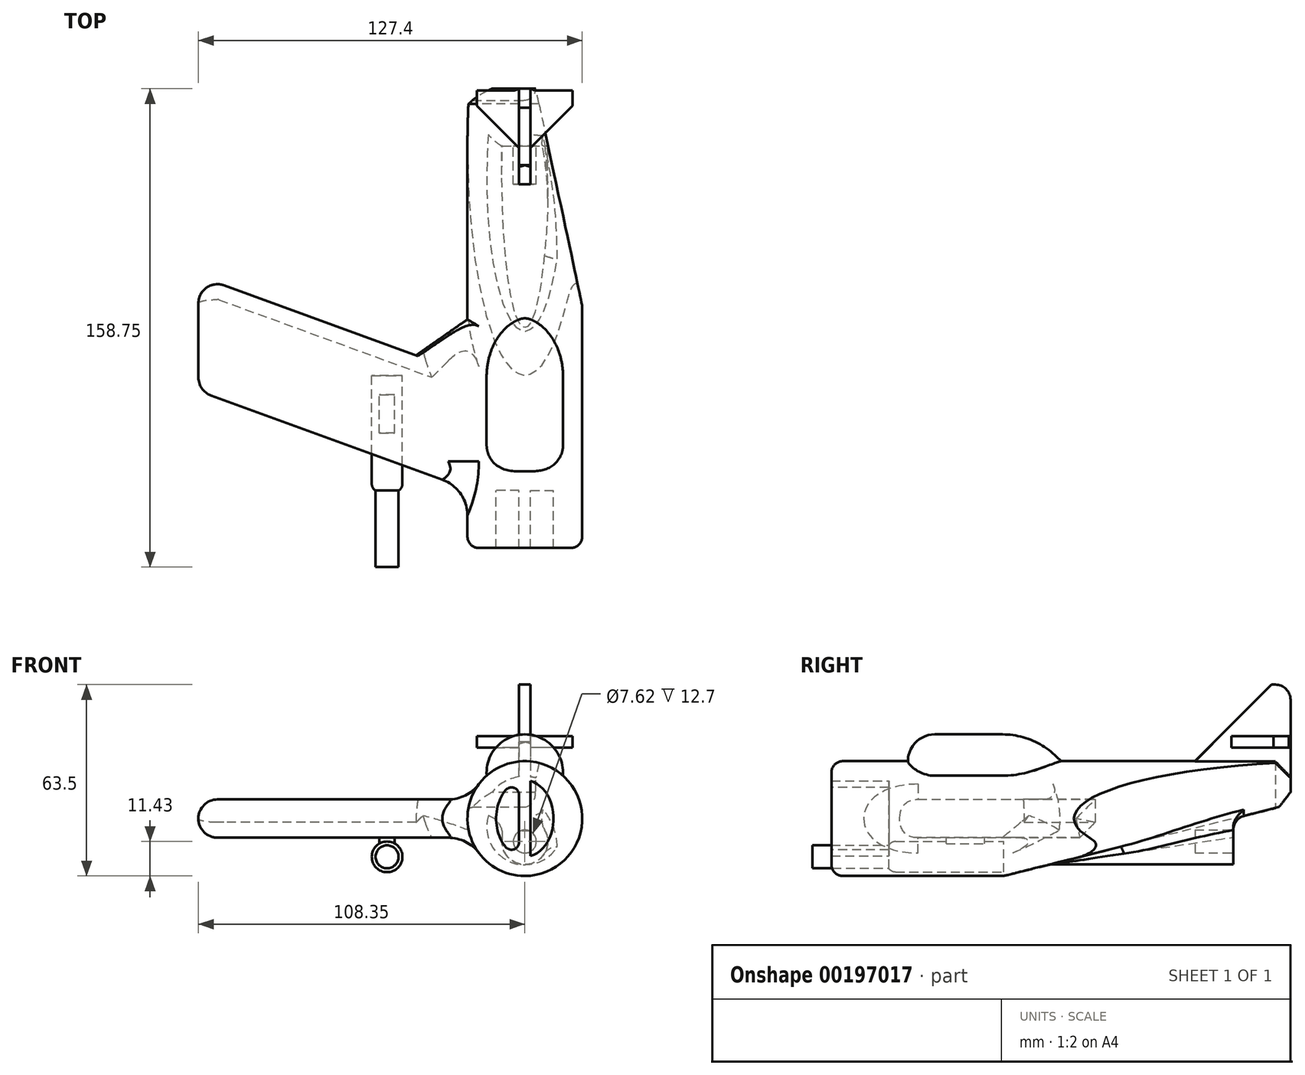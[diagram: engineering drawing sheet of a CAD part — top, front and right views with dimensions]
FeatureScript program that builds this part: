
annotation { "Feature Type Name" : "Feature", "Feature Type Description" : "" }
export const myFeature = defineFeature(function(context is Context, id is Id, definition is map)
    precondition{}
    {
        {
            var Q0;
            Q0=qCreatedBy(makeId("Front.planeOp"),FACE);
            var sketch = newSketch(context, id + "F0", { "sketchPlane" : qUnion([Q0])});
            skCircle(sketch, "E0", {"center": v(0, 0) * mm, "radius": 19.05 * mm});
            skSolve(sketch);
        }
        {
            var Q0;
            Q0=makeQuery(id+"F0.imprint","IMPRINT",FACE,{"disambiguationData":[TD([[makeQuery(id+"F0.imprint","IMPRINT",EDGE,{"derivedFrom":sQuery(id+"F0.wireOp",EDGE,"E0")}),1.0]])]});
            extrude(context, id + "F1", {"entities" : qUnion([Q0]), "endBound" : BoundingType.SYMMETRIC, "depth" : 152.4 * mm});
        }
        {
            var Q0;
            Q0=qCreatedBy(makeId("Top.planeOp"),FACE);
            var sketch = newSketch(context, id + "F2", { "sketchPlane" : qUnion([Q0])});
            skLineSegment(sketch, "E1", {"start": v(0, -25.4) * mm, "end": v(0, -63.5) * mm});
            skLineSegment(sketch, "E2", {"start": v(0, -63.5) * mm, "end": v(-108.35, -24.06) * mm});
            skLineSegment(sketch, "E3", {"start": v(-108.35, -24.06) * mm, "end": v(-108.35, 14.04) * mm});
            skLineSegment(sketch, "E4", {"start": v(-108.35, 14.04) * mm, "end": v(0, -25.4) * mm});
            skSolve(sketch);
        }
        {
            var Q0;
            Q0 = qSketchRegion(id + "F2", true);
            extrude(context, id + "F3", {"entities" : qUnion([Q0]), "operationType" : NewBodyOperationType.ADD, "endBound" : BoundingType.SYMMETRIC, "depth" : 12.7 * mm});
        }
        {
            var Q0;
            Q0=makeQuery(id+"F3.opExtrude","CAP_EDGE",EDGE,{"disambiguationData":[OSD([sQuery(id+"F2.wireOp",EDGE,"E2")])],"isStart":false});
            var Q1;
            Q1=makeQuery(id+"F3.opExtrude","CAP_EDGE",EDGE,{"disambiguationData":[OSD([sQuery(id+"F2.wireOp",EDGE,"E2")])],"isStart":true});
            var Q2;
            Q2=makeQuery(id+"F3.opExtrude","SWEPT_FACE",FACE,{"disambiguationData":[OSD([sQuery(id+"F2.wireOp",EDGE,"E3")])]});
            fillet(context, id + "F4", {"entities" : qUnion([Q0, Q1, Q2]), "radius" : 6.35 * mm, "tangentPropagation" : true, "allowEdgeOverflow" : false});
        }
        {
            var Q0;
            Q0=makeQuery(id+"F3.opExtrude","CAP_EDGE",EDGE,{"disambiguationData":[OSD([sQuery(id+"F2.wireOp",EDGE,"E4")])],"isStart":true});
            chamfer(context, id + "F5", {"entities" : qUnion([Q0]), "width" : 5.08 * mm, "tangentPropagation" : true});
        }
        {
            var Q0;
            Q0=qCreatedBy(makeId("Right.planeOp"),FACE);
            var sketch = newSketch(context, id + "F6", { "sketchPlane" : qUnion([Q0])});
            skLineSegment(sketch, "E5", {"start": v(82.55, 6.35) * mm, "end": v(82.55, -25.4) * mm});
            skLineSegment(sketch, "E6", {"start": v(82.55, -25.4) * mm, "end": v(-44.45, -25.4) * mm});
            skLineSegment(sketch, "E7", {"start": v(-44.45, -25.4) * mm, "end": v(82.55, 6.35) * mm});
            skSolve(sketch);
        }
        {
            var Q0;
            Q0 = qSketchRegion(id + "F6", true);
            extrude(context, id + "F7", {"entities" : qUnion([Q0]), "operationType" : NewBodyOperationType.REMOVE, "endBound" : BoundingType.SYMMETRIC, "depth" : 76.2 * mm});
        }
        {
            var Q0;
            Q0=qCreatedBy(makeId("Front.planeOp"),FACE);
            var sketch = newSketch(context, id + "F8", { "sketchPlane" : qUnion([Q0])});
            skCircle(sketch, "E8", {"center": v(0, 15.24) * mm, "radius": 12.7 * mm});
            skSolve(sketch);
        }
        {
            var Q0;
            Q0=makeQuery(id+"F8.imprint","IMPRINT",FACE,{"disambiguationData":[TD([[makeQuery(id+"F8.imprint","IMPRINT",EDGE,{"derivedFrom":sQuery(id+"F8.wireOp",EDGE,"E8")}),1.0]])]});
            extrude(context, id + "F9", {"entities" : qUnion([Q0]), "operationType" : NewBodyOperationType.ADD, "depth" : 50.8 * mm});
        }
        {
            var Q0;
            Q0=makeQuery(id+"F9.opExtrude","CAP_EDGE",EDGE,{"disambiguationData":[OSD([sQuery(id+"F8.wireOp",EDGE,"E8")])],"isStart":true});
            chamfer(context, id + "F10", {"entities" : qUnion([Q0]), "width" : 8.9 * mm, "tangentPropagation" : true});
        }
        {
            var Q0;
            Q0=makeQuery(id+"F9.opExtrude","CAP_EDGE",EDGE,{"disambiguationData":[OSD([sQuery(id+"F8.wireOp",EDGE,"E8")])],"isStart":false});
            fillet(context, id + "F11", {"entities" : qUnion([Q0]), "radius" : 8.9 * mm, "tangentPropagation" : true, "allowEdgeOverflow" : false});
        }
        {
            var Q0;
            {var subQ0=sQuery(id+"F8.wireOp",EDGE,"E8");Q0=makeQuery(id+"F10.opChamfer","BLEND_EDGE",EDGE,{"blendedFrom":[makeQuery(id+"F9.opExtrude","CAP_EDGE",EDGE,{"disambiguationData":[OSD([subQ0])],"isStart":true}),makeQuery(id+"F9.opExtrude","SWEPT_FACE",FACE,{"disambiguationData":[OSD([subQ0])]})],"blendedInto":[makeQuery(id+"F9.opExtrude","SWEPT_FACE",FACE,{"disambiguationData":[OSD([subQ0])]})]});}
            fillet(context, id + "F12", {"entities" : qUnion([Q0]), "radius" : 25.4 * mm, "tangentPropagation" : true, "allowEdgeOverflow" : false});
        }
        {
            var Q0;
            Q0=makeQuery(id+"F1.opExtrude","CAP_FACE",FACE,{"disambiguationData":[OSD([sQuery(id+"F0.wireOp",EDGE,"E0")])],"isStart":true});
            var sketch = newSketch(context, id + "F13", { "sketchPlane" : qUnion([Q0])});
            skLineSegment(sketch, "E9.bottom", {"start": v(-1.9, 44.45) * mm, "end": v(1.9, 44.45) * mm});
            skLineSegment(sketch, "E9.top", {"start": v(-1.9, 6.35) * mm, "end": v(1.9, 6.35) * mm});
            skLineSegment(sketch, "E9.left", {"start": v(-1.9, 44.45) * mm, "end": v(-1.9, 6.35) * mm});
            skLineSegment(sketch, "E9.right", {"start": v(1.9, 44.45) * mm, "end": v(1.9, 6.35) * mm});
            skPoint(sketch, "E9.middle", {"position": v(0, 25.4) * mm});
            skSolve(sketch);
        }
        {
            var Q0;
            Q0 = qSketchRegion(id + "F13", true);
            extrude(context, id + "F14", {"entities" : qUnion([Q0]), "operationType" : NewBodyOperationType.ADD, "oppositeDirection" : true, "depth" : 25.4 * mm});
        }
        {
            var Q0;
            Q0=makeQuery(id+"F14.opExtrude","CAP_EDGE",EDGE,{"disambiguationData":[OSD([sQuery(id+"F13.wireOp",EDGE,"E9.bottom")])],"isStart":false});
            chamfer(context, id + "F15", {"entities" : qUnion([Q0]), "width" : 19.05 * mm, "tangentPropagation" : true});
        }
        {
            var Q0;
            Q0=makeQuery(id+"F14.opExtrude","CAP_EDGE",EDGE,{"disambiguationData":[OSD([sQuery(id+"F13.wireOp",EDGE,"E9.bottom")])],"isStart":true});
            fillet(context, id + "F16", {"entities" : qUnion([Q0]), "radius" : 5.08 * mm, "tangentPropagation" : true, "allowEdgeOverflow" : false});
        }
        {
            var Q0;
            Q0=qCreatedBy(makeId("Right.planeOp"),FACE);
            var sketch = newSketch(context, id + "F17", { "sketchPlane" : qUnion([Q0])});
            skLineSegment(sketch, "E10.bottom", {"start": v(75.56, 27.3) * mm, "end": v(56.52, 27.3) * mm});
            skLineSegment(sketch, "E10.top", {"start": v(75.57, 23.5) * mm, "end": v(56.52, 23.5) * mm});
            skLineSegment(sketch, "E10.left", {"start": v(75.57, 27.3) * mm, "end": v(75.57, 23.5) * mm});
            skLineSegment(sketch, "E10.right", {"start": v(56.52, 27.3) * mm, "end": v(56.52, 23.5) * mm});
            skPoint(sketch, "E10.middle", {"position": v(66.04, 25.4) * mm});
            skSolve(sketch);
        }
        {
            var Q0;
            Q0 = qSketchRegion(id + "F17", true);
            extrude(context, id + "F18", {"entities" : qUnion([Q0]), "operationType" : NewBodyOperationType.ADD, "endBound" : BoundingType.SYMMETRIC, "depth" : 31.75 * mm});
        }
        {
            var Q0;
            Q0=makeQuery(id+"F18.opExtrude","CAP_EDGE",EDGE,{"disambiguationData":[OSD([sQuery(id+"F17.wireOp",EDGE,"E10.right")])],"isStart":true});
            var Q1;
            Q1=makeQuery(id+"F18.opExtrude","CAP_EDGE",EDGE,{"disambiguationData":[OSD([sQuery(id+"F17.wireOp",EDGE,"E10.right")])],"isStart":false});
            chamfer(context, id + "F19", {"entities" : qUnion([Q0, Q1]), "width" : 13.97 * mm, "tangentPropagation" : true});
        }
        {
            var Q0;
            Q0=makeQuery(id+"F1.opExtrude","CAP_FACE",FACE,{"disambiguationData":[OSD([sQuery(id+"F0.wireOp",EDGE,"E0")])],"isStart":false});
            var sketch = newSketch(context, id + "F20", { "sketchPlane" : qUnion([Q0])});
            skEllipse(sketch, "E11", {"center": v(0, 0) * mm, "majorRadius": 12.7 * mm, "minorRadius": 9.53 * mm, "majorAxis": v(0, 1)});
            skSolve(sketch);
        }
        {
            var Q0;
            Q0=makeQuery(id+"F20.imprint","IMPRINT",FACE,{"disambiguationData":[TD([[makeQuery(id+"F20.imprint","IMPRINT",EDGE,{"derivedFrom":sQuery(id+"F20.wireOp",EDGE,"E11")}),1.0]])]});
            extrude(context, id + "F21", {"entities" : qUnion([Q0]), "operationType" : NewBodyOperationType.REMOVE, "oppositeDirection" : true, "depth" : 25.4 * mm});
        }
        {
            var Q0;
            Q0=makeQuery(id+"F1.opExtrude","CAP_EDGE",EDGE,{"disambiguationData":[OSD([sQuery(id+"F0.wireOp",EDGE,"E0")])],"isStart":false});
            fillet(context, id + "F22", {"entities" : qUnion([Q0]), "radius" : 3.8 * mm, "tangentPropagation" : true, "allowEdgeOverflow" : false});
        }
        {
            var Q0;
            Q0=makeQuery(id+"F21.boolean.opBoolean","COPY",FACE,{"derivedFrom":makeQuery(id+"F21.opExtrude","CAP_FACE",FACE,{"disambiguationData":[OSD([sQuery(id+"F20.wireOp",EDGE,"E11")])],"isStart":false})});
            var sketch = newSketch(context, id + "F23", { "sketchPlane" : qUnion([Q0])});
            skLineSegment(sketch, "E12.bottom", {"start": v(1.9, 15.24) * mm, "end": v(-1.9, 15.24) * mm});
            skLineSegment(sketch, "E12.top", {"start": v(1.9, -15.24) * mm, "end": v(-1.9, -15.24) * mm});
            skLineSegment(sketch, "E12.left", {"start": v(1.9, 15.24) * mm, "end": v(1.9, -15.24) * mm});
            skLineSegment(sketch, "E12.right", {"start": v(-1.9, 15.24) * mm, "end": v(-1.9, -15.24) * mm});
            skPoint(sketch, "E12.middle", {"position": v(0, 0) * mm});
            skSolve(sketch);
        }
        {
            var Q0;
            {var subQ0=sQuery(id+"F23.wireOp",EDGE,"E12.left");var subQ1=makeQuery(id+"F21.boolean.opBoolean","COPY",EDGE,{"derivedFrom":makeQuery(id+"F21.opExtrude","CAP_EDGE",EDGE,{"disambiguationData":[OSD([sQuery(id+"F20.wireOp",EDGE,"E11")])],"isStart":false})});var subQ2=makeQuery(id+"F23.imprint","INTERSECT",VERTEX,{"disambiguationData":[OD(0.0)],"derivedFrom":[subQ1,subQ0]});Q0=makeQuery(id+"F23.imprint","IMPRINT",FACE,{"disambiguationData":[TD([[makeQuery(id+"F23.imprint","IMPRINT",EDGE,{"disambiguationData":[TD([[subQ2,-1.0]])],"derivedFrom":subQ0}),-1.0]])]});}
            extrude(context, id + "F24", {"entities" : qUnion([Q0]), "operationType" : NewBodyOperationType.ADD, "depth" : 25.4 * mm});
        }
        {
            var Q0;
            {var subQ0=sQuery(id+"F23.wireOp",EDGE,"E12.left");var subQ1=sQuery(id+"F20.wireOp",EDGE,"E11");Q0=makeQuery(id+"F24.opExtrude","SWEPT_EDGE",EDGE,{"disambiguationData":[OSD([subQ1,subQ0]),TDD([makeQuery(id+"F23.imprint","INTERSECT",VERTEX,{"disambiguationData":[OD(0.0)],"derivedFrom":[makeQuery(id+"F21.boolean.opBoolean","COPY",EDGE,{"derivedFrom":makeQuery(id+"F21.opExtrude","CAP_EDGE",EDGE,{"disambiguationData":[OSD([subQ1])],"isStart":false})}),subQ0]})])]});}
            var Q1;
            {var subQ0=sQuery(id+"F23.wireOp",EDGE,"E12.right");var subQ1=sQuery(id+"F20.wireOp",EDGE,"E11");Q1=makeQuery(id+"F24.opExtrude","SWEPT_EDGE",EDGE,{"disambiguationData":[OSD([subQ1,subQ0]),TDD([makeQuery(id+"F23.imprint","INTERSECT",VERTEX,{"disambiguationData":[OD(0.0)],"derivedFrom":[makeQuery(id+"F21.boolean.opBoolean","COPY",EDGE,{"derivedFrom":makeQuery(id+"F21.opExtrude","CAP_EDGE",EDGE,{"disambiguationData":[OSD([subQ1])],"isStart":false})}),subQ0]})])]});}
            var Q2;
            {var subQ0=sQuery(id+"F23.wireOp",EDGE,"E12.left");var subQ1=sQuery(id+"F20.wireOp",EDGE,"E11");Q2=makeQuery(id+"F24.opExtrude","SWEPT_EDGE",EDGE,{"disambiguationData":[OSD([subQ1,subQ0]),TDD([makeQuery(id+"F23.imprint","INTERSECT",VERTEX,{"disambiguationData":[OD(1.0)],"derivedFrom":[makeQuery(id+"F21.boolean.opBoolean","COPY",EDGE,{"derivedFrom":makeQuery(id+"F21.opExtrude","CAP_EDGE",EDGE,{"disambiguationData":[OSD([subQ1])],"isStart":false})}),subQ0]})])]});}
            var Q3;
            {var subQ0=sQuery(id+"F23.wireOp",EDGE,"E12.right");var subQ1=sQuery(id+"F20.wireOp",EDGE,"E11");Q3=makeQuery(id+"F24.opExtrude","SWEPT_EDGE",EDGE,{"disambiguationData":[OSD([subQ1,subQ0]),TDD([makeQuery(id+"F23.imprint","INTERSECT",VERTEX,{"disambiguationData":[OD(1.0)],"derivedFrom":[makeQuery(id+"F21.boolean.opBoolean","COPY",EDGE,{"derivedFrom":makeQuery(id+"F21.opExtrude","CAP_EDGE",EDGE,{"disambiguationData":[OSD([subQ1])],"isStart":false})}),subQ0]})])]});}
            fillet(context, id + "F25", {"entities" : qUnion([Q0, Q1, Q2, Q3]), "radius" : 2.54 * mm, "tangentPropagation" : true, "allowEdgeOverflow" : false});
        }
        {
            var Q0;
            {var subQ0=sQuery(id+"F13.wireOp",EDGE,"E9.right");var subQ1=sQuery(id+"F0.wireOp",EDGE,"E0");Q0=makeQuery(id+"F14.boolean.opBoolean","SPLIT",EDGE,{"disambiguationData":[TD([makeQuery(id+"F14.opExtrude","SWEPT_FACE",FACE,{"disambiguationData":[OSD([subQ0])]})])],"derivedFrom":makeQuery(id+"F1.opExtrude","CAP_EDGE",EDGE,{"disambiguationData":[OSD([subQ1])],"isStart":true})});}
            var Q1;
            {var subQ0=sQuery(id+"F13.wireOp",EDGE,"E9.left");var subQ1=sQuery(id+"F0.wireOp",EDGE,"E0");Q1=makeQuery(id+"F14.boolean.opBoolean","SPLIT",EDGE,{"disambiguationData":[TD([makeQuery(id+"F14.opExtrude","SWEPT_FACE",FACE,{"disambiguationData":[OSD([subQ0])]})])],"derivedFrom":makeQuery(id+"F1.opExtrude","CAP_EDGE",EDGE,{"disambiguationData":[OSD([subQ1])],"isStart":true})});}
            var Q2;
            Q2=makeQuery(id+"F7.boolean.opBoolean","INTERSECT",EDGE,{"derivedFrom":[makeQuery(id+"F1.opExtrude","CAP_FACE",FACE,{"disambiguationData":[OSD([sQuery(id+"F0.wireOp",EDGE,"E0")])],"isStart":true}),makeQuery(id+"F7.opExtrude","SWEPT_FACE",FACE,{"disambiguationData":[OSD([sQuery(id+"F6.wireOp",EDGE,"E7")])]})]});
            chamfer(context, id + "F26", {"entities" : qUnion([Q0, Q1, Q2]), "width" : 5.08 * mm, "tangentPropagation" : true});
        }
        {
            var Q0;
            Q0=qCreatedBy(makeId("Top.planeOp"),FACE);
            var sketch = newSketch(context, id + "F27", { "sketchPlane" : qUnion([Q0])});
            skLineSegment(sketch, "E13", {"start": v(2.54, 81.28) * mm, "end": v(21.59, 81.28) * mm});
            skLineSegment(sketch, "E14", {"start": v(21.59, 81.28) * mm, "end": v(21.6, -7.62) * mm});
            skLineSegment(sketch, "E15", {"start": v(21.6, -7.62) * mm, "end": v(2.54, 81.28) * mm});
            skSolve(sketch);
        }
        {
            var Q0;
            Q0 = qSketchRegion(id + "F27", true);
            extrude(context, id + "F28", {"entities" : qUnion([Q0]), "operationType" : NewBodyOperationType.REMOVE, "endBound" : BoundingType.SYMMETRIC, "oppositeDirection" : true, "depth" : 38.1 * mm});
        }
        {
            var Q0;
            Q0=makeQuery(id+"FcNdPO8GNdQ5qAE_1.1.F3.boolean.opBoolean","INTERSECT",EDGE,{"derivedFrom":[makeQuery(id+"F1.opExtrude","SWEPT_FACE",FACE,{"disambiguationData":[OSD([sQuery(id+"F0.wireOp",EDGE,"E0")])]}),makeQuery(id+"FcNdPO8GNdQ5qAE_1.1.F3.opExtrude","CAP_FACE",FACE,{"disambiguationData":[OSD([sQuery(id+"F2.wireOp",EDGE,"E1"),sQuery(id+"F2.wireOp",EDGE,"E2"),sQuery(id+"F2.wireOp",EDGE,"E3"),sQuery(id+"F2.wireOp",EDGE,"E4")])],"isStart":true})]});
            var Q1;
            Q1=makeQuery(id+"F3.boolean.opBoolean","INTERSECT",EDGE,{"derivedFrom":[makeQuery(id+"F1.opExtrude","SWEPT_FACE",FACE,{"disambiguationData":[OSD([sQuery(id+"F0.wireOp",EDGE,"E0")])]}),makeQuery(id+"F3.opExtrude","CAP_FACE",FACE,{"disambiguationData":[OSD([sQuery(id+"F2.wireOp",EDGE,"E1"),sQuery(id+"F2.wireOp",EDGE,"E2"),sQuery(id+"F2.wireOp",EDGE,"E3"),sQuery(id+"F2.wireOp",EDGE,"E4")])],"isStart":false})]});
            fillet(context, id + "F29", {"entities" : qUnion([Q0, Q1]), "radius" : 12.7 * mm, "tangentPropagation" : true, "allowEdgeOverflow" : false});
        }
        {
            var Q0;
            Q0=makeQuery(id+"F28.boolean.opBoolean","INTERSECT",EDGE,{"derivedFrom":[makeQuery(id+"F7.boolean.opBoolean","COPY",FACE,{"derivedFrom":makeQuery(id+"F7.opExtrude","SWEPT_FACE",FACE,{"disambiguationData":[OSD([sQuery(id+"F6.wireOp",EDGE,"E7")])]})}),makeQuery(id+"F28.opExtrude","SWEPT_FACE",FACE,{"disambiguationData":[OSD([sQuery(id+"F27.wireOp",EDGE,"E15")])]})]});
            var Q1;
            Q1=makeQuery(id+"FuSagtjNPapZBO8_1.1.F28.boolean.opBoolean","INTERSECT",EDGE,{"derivedFrom":[makeQuery(id+"F7.boolean.opBoolean","COPY",FACE,{"derivedFrom":makeQuery(id+"F7.opExtrude","SWEPT_FACE",FACE,{"disambiguationData":[OSD([sQuery(id+"F6.wireOp",EDGE,"E7")])]})}),makeQuery(id+"FuSagtjNPapZBO8_1.1.F28.opExtrude","SWEPT_FACE",FACE,{"disambiguationData":[OSD([sQuery(id+"F27.wireOp",EDGE,"E15")])]})]});
            fillet(context, id + "F30", {"entities" : qUnion([Q0, Q1]), "radius" : 5.08 * mm, "tangentPropagation" : true, "allowEdgeOverflow" : false});
        }
        {
            var Q0;
            Q0=qCreatedBy(makeId("Front.planeOp"),FACE);
            var sketch = newSketch(context, id + "F31", { "sketchPlane" : qUnion([Q0])});
            skCircle(sketch, "E16", {"center": v(0, -7.62) * mm, "radius": 7.62 * mm});
            skSolve(sketch);
        }
        {
            var Q0;
            Q0 = qSketchRegion(id + "F31", true);
            extrude(context, id + "F32", {"entities" : qUnion([Q0]), "operationType" : NewBodyOperationType.ADD, "endBound" : BoundingType.SYMMETRIC, "depth" : 114.3 * mm});
        }
        {
            var Q0;
            {var subQ0=sQuery(id+"F20.wireOp",EDGE,"E11");Q0=makeQuery(id+"F24.boolean.opBoolean","SPLIT",FACE,{"disambiguationData":[TD([makeQuery(id+"F24.opExtrude","SWEPT_FACE",FACE,{"disambiguationData":[OSD([sQuery(id+"F23.wireOp",EDGE,"E12.right")])]})])],"derivedFrom":makeQuery(id+"F21.boolean.opBoolean","COPY",FACE,{"derivedFrom":makeQuery(id+"F21.opExtrude","CAP_FACE",FACE,{"disambiguationData":[OSD([subQ0])],"isStart":false})})});}
            var Q1;
            {var subQ0=sQuery(id+"F20.wireOp",EDGE,"E11");Q1=makeQuery(id+"F24.boolean.opBoolean","SPLIT",FACE,{"disambiguationData":[TD([makeQuery(id+"F24.opExtrude","SWEPT_FACE",FACE,{"disambiguationData":[OSD([sQuery(id+"F23.wireOp",EDGE,"E12.left")])]})])],"derivedFrom":makeQuery(id+"F21.boolean.opBoolean","COPY",FACE,{"derivedFrom":makeQuery(id+"F21.opExtrude","CAP_FACE",FACE,{"disambiguationData":[OSD([subQ0])],"isStart":false})})});}
            extrude(context, id + "F33", {"entities" : qUnion([Q0, Q1]), "operationType" : NewBodyOperationType.ADD, "depth" : 6.35 * mm});
        }
        {
            var Q0;
            Q0=makeQuery(id+"F32.boolean.opBoolean","INTERSECT",EDGE,{"disambiguationData":[OD(0.0)],"derivedFrom":[makeQuery(id+"F7.boolean.opBoolean","COPY",FACE,{"derivedFrom":makeQuery(id+"F7.opExtrude","SWEPT_FACE",FACE,{"disambiguationData":[OSD([sQuery(id+"F6.wireOp",EDGE,"E7")])]})}),makeQuery(id+"F32.opExtrude","SWEPT_FACE",FACE,{"disambiguationData":[OSD([sQuery(id+"F31.wireOp",EDGE,"E16")])]})]});
            fillet(context, id + "F34", {"entities" : qUnion([Q0]), "radius" : 5.08 * mm, "tangentPropagation" : true, "allowEdgeOverflow" : false});
        }
        {
            var Q0;
            Q0=makeQuery(id+"F32.opExtrude","CAP_FACE",FACE,{"disambiguationData":[OSD([sQuery(id+"F31.wireOp",EDGE,"E16")])],"isStart":true});
            var sketch = newSketch(context, id + "F35", { "sketchPlane" : qUnion([Q0])});
            skCircle(sketch, "E17", {"center": v(0, -7.62) * mm, "radius": 3.81 * mm});
            skSolve(sketch);
        }
        {
            var Q0;
            {var subQ0=sQuery(id+"F35.wireOp",EDGE,"E17");var subQ1=sQuery(id+"F31.wireOp",EDGE,"E16");var subQ2=makeQuery(id+"F34.opFillet","BLEND_EDGE",EDGE,{"disambiguationData":[OD(2.0)],"blendedFrom":[makeQuery(id+"F32.boolean.opBoolean","INTERSECT",EDGE,{"disambiguationData":[OD(1.0)],"derivedFrom":[makeQuery(id+"F7.boolean.opBoolean","COPY",FACE,{"derivedFrom":makeQuery(id+"F7.opExtrude","SWEPT_FACE",FACE,{"disambiguationData":[OSD([sQuery(id+"F6.wireOp",EDGE,"E7")])]})}),makeQuery(id+"F32.opExtrude","SWEPT_FACE",FACE,{"disambiguationData":[OSD([subQ1])]})]}),makeQuery(id+"F32.opExtrude","CAP_FACE",FACE,{"disambiguationData":[OSD([subQ1])],"isStart":true})],"blendedInto":[makeQuery(id+"F32.opExtrude","CAP_FACE",FACE,{"disambiguationData":[OSD([subQ1])],"isStart":true})]});var subQ3=makeQuery(id+"F35.imprint","INTERSECT",VERTEX,{"disambiguationData":[OD(0.0)],"derivedFrom":[subQ2,subQ0]});Q0=makeQuery(id+"F35.imprint","IMPRINT",FACE,{"disambiguationData":[TD([[makeQuery(id+"F35.imprint","IMPRINT",EDGE,{"disambiguationData":[TD([[subQ3,-1.0]])],"derivedFrom":subQ0}),1.0]])]});}
            var Q1;
            {var subQ0=sQuery(id+"F35.wireOp",EDGE,"E17");var subQ1=sQuery(id+"F31.wireOp",EDGE,"E16");var subQ2=makeQuery(id+"F34.opFillet","BLEND_EDGE",EDGE,{"disambiguationData":[OD(2.0)],"blendedFrom":[makeQuery(id+"F32.boolean.opBoolean","INTERSECT",EDGE,{"disambiguationData":[OD(1.0)],"derivedFrom":[makeQuery(id+"F7.boolean.opBoolean","COPY",FACE,{"derivedFrom":makeQuery(id+"F7.opExtrude","SWEPT_FACE",FACE,{"disambiguationData":[OSD([sQuery(id+"F6.wireOp",EDGE,"E7")])]})}),makeQuery(id+"F32.opExtrude","SWEPT_FACE",FACE,{"disambiguationData":[OSD([subQ1])]})]}),makeQuery(id+"F32.opExtrude","CAP_FACE",FACE,{"disambiguationData":[OSD([subQ1])],"isStart":true})],"blendedInto":[makeQuery(id+"F32.opExtrude","CAP_FACE",FACE,{"disambiguationData":[OSD([subQ1])],"isStart":true})]});var subQ3=makeQuery(id+"F35.imprint","INTERSECT",VERTEX,{"disambiguationData":[OD(0.0)],"derivedFrom":[subQ2,subQ0]});Q1=makeQuery(id+"F35.imprint","IMPRINT",FACE,{"disambiguationData":[TD([[makeQuery(id+"F35.imprint","IMPRINT",EDGE,{"disambiguationData":[TD([[subQ3,1.0]])],"derivedFrom":subQ0}),1.0]])]});}
            extrude(context, id + "F36", {"entities" : qUnion([Q0, Q1]), "operationType" : NewBodyOperationType.REMOVE, "oppositeDirection" : true, "depth" : 12.7 * mm});
        }
        {
            var Q0;
            Q0=makeQuery(id+"F18.boolean.opBoolean","INTERSECT",EDGE,{"derivedFrom":[makeQuery(id+"F14.opExtrude","SWEPT_FACE",FACE,{"disambiguationData":[OSD([sQuery(id+"F13.wireOp",EDGE,"E9.left")])]}),makeQuery(id+"F18.opExtrude","SWEPT_FACE",FACE,{"disambiguationData":[OSD([sQuery(id+"F17.wireOp",EDGE,"E10.left")])]})]});
            var Q1;
            Q1=makeQuery(id+"F18.boolean.opBoolean","INTERSECT",EDGE,{"derivedFrom":[makeQuery(id+"F14.opExtrude","SWEPT_FACE",FACE,{"disambiguationData":[OSD([sQuery(id+"F13.wireOp",EDGE,"E9.right")])]}),makeQuery(id+"F18.opExtrude","SWEPT_FACE",FACE,{"disambiguationData":[OSD([sQuery(id+"F17.wireOp",EDGE,"E10.left")])]})]});
            fillet(context, id + "F37", {"entities" : qUnion([Q0, Q1]), "radius" : 5.08 * mm, "tangentPropagation" : true, "allowEdgeOverflow" : false});
        }
        {
            var Q0;
            Q0=makeQuery(id+"F3.opExtrude","CAP_FACE",FACE,{"disambiguationData":[OSD([sQuery(id+"F2.wireOp",EDGE,"E1"),sQuery(id+"F2.wireOp",EDGE,"E2"),sQuery(id+"F2.wireOp",EDGE,"E3"),sQuery(id+"F2.wireOp",EDGE,"E4")])],"isStart":true});
            var sketch = newSketch(context, id + "F38", { "sketchPlane" : qUnion([Q0])});
            skLineSegment(sketch, "E18.bottom", {"start": v(-43.18, 38.1) * mm, "end": v(-48.26, 38.1) * mm});
            skLineSegment(sketch, "E18.top", {"start": v(-43.18, 25.4) * mm, "end": v(-48.26, 25.4) * mm});
            skLineSegment(sketch, "E18.left", {"start": v(-43.18, 38.1) * mm, "end": v(-43.18, 25.4) * mm});
            skLineSegment(sketch, "E18.right", {"start": v(-48.26, 38.1) * mm, "end": v(-48.26, 25.4) * mm});
            skSolve(sketch);
        }
        {
            var Q0;
            Q0=makeQuery(id+"F38.imprint","IMPRINT",FACE,{"disambiguationData":[TD([[makeQuery(id+"F38.imprint","IMPRINT",EDGE,{"derivedFrom":sQuery(id+"F38.wireOp",EDGE,"E18.bottom")}),1.0]])]});
            extrude(context, id + "F39", {"entities" : qUnion([Q0]), "operationType" : NewBodyOperationType.ADD, "depth" : 5.08 * mm});
        }
        {
            var Q0;
            Q0=makeQuery(id+"F39.opExtrude","SWEPT_FACE",FACE,{"disambiguationData":[OSD([sQuery(id+"F38.wireOp",EDGE,"E18.bottom")])]});
            var sketch = newSketch(context, id + "F40", { "sketchPlane" : qUnion([Q0])});
            skCircle(sketch, "E19", {"center": v(-45.72, -12.7) * mm, "radius": 5.08 * mm});
            skPoint(sketch, "E19.centerSnap0", {"position": v(-45.72, -11.43) * mm});
            skSolve(sketch);
        }
        {
            var Q0;
            Q0 = qSketchRegion(id + "F40", true);
            extrude(context, id + "F41", {"entities" : qUnion([Q0]), "operationType" : NewBodyOperationType.ADD, "endBound" : BoundingType.SYMMETRIC, "depth" : 38.1 * mm});
        }
        {
            var Q0;
            Q0=makeQuery(id+"F41.opExtrude","CAP_FACE",FACE,{"disambiguationData":[OSD([sQuery(id+"F40.wireOp",EDGE,"E19")])],"isStart":false});
            var sketch = newSketch(context, id + "F42", { "sketchPlane" : qUnion([Q0])});
            skCircle(sketch, "E20", {"center": v(-45.72, -12.7) * mm, "radius": 3.8 * mm});
            skSolve(sketch);
        }
        {
            var Q0;
            Q0=makeQuery(id+"F42.imprint","IMPRINT",FACE,{"disambiguationData":[TD([[makeQuery(id+"F42.imprint","IMPRINT",EDGE,{"derivedFrom":sQuery(id+"F42.wireOp",EDGE,"E20")}),1.0]])]});
            extrude(context, id + "F43", {"entities" : qUnion([Q0]), "operationType" : NewBodyOperationType.ADD, "depth" : 25.4 * mm});
        }
        {
            var Q0;
            Q0=makeQuery(id+"F3.boolean.opBoolean","INTERSECT",EDGE,{"derivedFrom":[makeQuery(id+"F1.opExtrude","SWEPT_FACE",FACE,{"disambiguationData":[OSD([sQuery(id+"F0.wireOp",EDGE,"E0")])]}),makeQuery(id+"F3.opExtrude","SWEPT_FACE",FACE,{"disambiguationData":[OSD([sQuery(id+"F2.wireOp",EDGE,"E4")])]})]});
            var Q1;
            Q1=makeQuery(id+"FcNdPO8GNdQ5qAE_1.1.F3.boolean.opBoolean","INTERSECT",EDGE,{"derivedFrom":[makeQuery(id+"F1.opExtrude","SWEPT_FACE",FACE,{"disambiguationData":[OSD([sQuery(id+"F0.wireOp",EDGE,"E0")])]}),makeQuery(id+"FcNdPO8GNdQ5qAE_1.1.F3.opExtrude","SWEPT_FACE",FACE,{"disambiguationData":[OSD([sQuery(id+"F2.wireOp",EDGE,"E4")])]})]});
            var Q2;
            Q2=makeQuery(id+"FcNdPO8GNdQ5qAE_1.1.F5.opChamfer","BLEND_EDGE",EDGE,{"blendedFrom":[makeQuery(id+"FcNdPO8GNdQ5qAE_1.1.F3.opExtrude","CAP_EDGE",EDGE,{"disambiguationData":[OSD([sQuery(id+"F2.wireOp",EDGE,"E4")])],"isStart":true}),makeQuery(id+"F1.opExtrude","SWEPT_FACE",FACE,{"disambiguationData":[OSD([sQuery(id+"F0.wireOp",EDGE,"E0")])]})],"blendedInto":[makeQuery(id+"F1.opExtrude","SWEPT_FACE",FACE,{"disambiguationData":[OSD([sQuery(id+"F0.wireOp",EDGE,"E0")])]})]});
            var Q3;
            Q3=makeQuery(id+"F5.opChamfer","BLEND_EDGE",EDGE,{"blendedFrom":[makeQuery(id+"F3.opExtrude","CAP_EDGE",EDGE,{"disambiguationData":[OSD([sQuery(id+"F2.wireOp",EDGE,"E4")])],"isStart":true}),makeQuery(id+"F1.opExtrude","SWEPT_FACE",FACE,{"disambiguationData":[OSD([sQuery(id+"F0.wireOp",EDGE,"E0")])]})],"blendedInto":[makeQuery(id+"F1.opExtrude","SWEPT_FACE",FACE,{"disambiguationData":[OSD([sQuery(id+"F0.wireOp",EDGE,"E0")])]})]});
            chamfer(context, id + "F44", {"entities" : qUnion([Q0, Q1, Q2, Q3]), "width" : 12.7 * mm, "tangentPropagation" : true});
        }
        {
            var Q0;
            Q0=makeQuery(id+"F14.boolean.opBoolean","INTERSECT",EDGE,{"derivedFrom":[makeQuery(id+"F1.opExtrude","SWEPT_FACE",FACE,{"disambiguationData":[OSD([sQuery(id+"F0.wireOp",EDGE,"E0")])]}),makeQuery(id+"F14.opExtrude","CAP_FACE",FACE,{"disambiguationData":[OSD([sQuery(id+"F13.wireOp",EDGE,"E9.bottom"),sQuery(id+"F13.wireOp",EDGE,"E9.top"),sQuery(id+"F13.wireOp",EDGE,"E9.left"),sQuery(id+"F13.wireOp",EDGE,"E9.right")])],"isStart":false})]});
            chamfer(context, id + "F45", {"entities" : qUnion([Q0]), "width" : 6.35 * mm, "tangentPropagation" : true});
        }
        {
            var Q0;
            {var subQ0=makeQuery(id+"F14.opExtrude","CAP_FACE",FACE,{"disambiguationData":[OSD([sQuery(id+"F13.wireOp",EDGE,"E9.bottom"),sQuery(id+"F13.wireOp",EDGE,"E9.top"),sQuery(id+"F13.wireOp",EDGE,"E9.left"),sQuery(id+"F13.wireOp",EDGE,"E9.right")])],"isStart":false});Q0=makeQuery(id+"F45.opChamfer","BLEND_EDGE",EDGE,{"disambiguationData":[OD(1.0)],"blendedFrom":[makeQuery(id+"F14.boolean.opBoolean","INTERSECT",EDGE,{"derivedFrom":[makeQuery(id+"F1.opExtrude","SWEPT_FACE",FACE,{"disambiguationData":[OSD([sQuery(id+"F0.wireOp",EDGE,"E0")])]}),subQ0]}),subQ0],"blendedInto":[subQ0]});}
            fillet(context, id + "F46", {"entities" : qUnion([Q0]), "radius" : 5.08 * mm, "tangentPropagation" : true, "allowEdgeOverflow" : false});
        }
        {
            var Q0;
            Q0=makeQuery(id+"FNYXOjzqiPna6Tf_1.1.F41.opExtrude","CAP_EDGE",EDGE,{"disambiguationData":[OSD([sQuery(id+"F40.wireOp",EDGE,"E19")])],"isStart":false});
            var Q1;
            Q1=makeQuery(id+"F41.opExtrude","CAP_EDGE",EDGE,{"disambiguationData":[OSD([sQuery(id+"F40.wireOp",EDGE,"E19")])],"isStart":false});
            fillet(context, id + "F47", {"entities" : qUnion([Q0, Q1]), "radius" : 2.54 * mm, "tangentPropagation" : true, "allowEdgeOverflow" : false});
        }
    });
